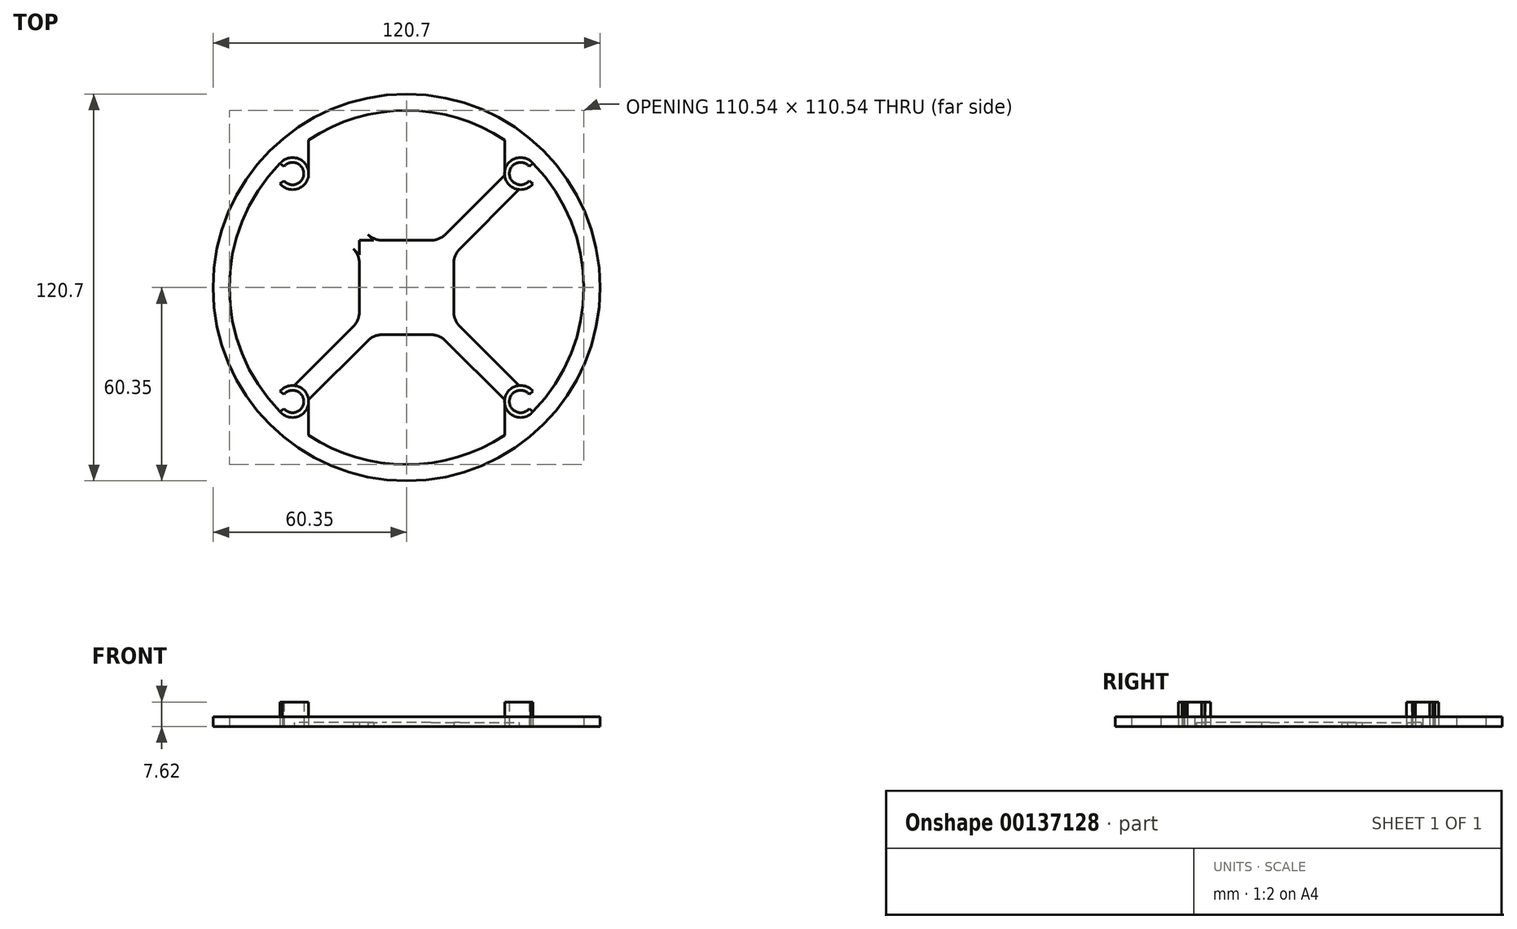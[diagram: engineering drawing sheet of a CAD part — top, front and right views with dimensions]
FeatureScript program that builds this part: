
annotation { "Feature Type Name" : "Feature", "Feature Type Description" : "" }
export const myFeature = defineFeature(function(context is Context, id is Id, definition is map)
    precondition{}
    {
        {
            var Q0;
            Q0=qCreatedBy(makeId("Top.planeOp"),FACE);
            var sketch = newSketch(context, id + "F0", { "sketchPlane" : qUnion([Q0])});
            skLineSegment(sketch, "E0.bottom", {"start": v(35.56, 35.56) * mm, "end": v(-35.56, 35.56) * mm});
            skLineSegment(sketch, "E0.top", {"start": v(35.56, -35.56) * mm, "end": v(-35.56, -35.56) * mm});
            skLineSegment(sketch, "E0.left", {"start": v(35.56, 35.56) * mm, "end": v(35.56, -35.56) * mm});
            skLineSegment(sketch, "E0.right", {"start": v(-35.56, 35.56) * mm, "end": v(-35.56, -35.56) * mm});
            skPoint(sketch, "E0.middle", {"position": v(0, 0) * mm});
            skLineSegment(sketch, "E1", {"start": v(0, 35.56) * mm, "end": v(0, -35.56) * mm, "construction": true});
            skCircle(sketch, "E2", {"center": v(35.56, 35.56) * mm, "radius": 3.5 * mm});
            skCircle(sketch, "E3", {"center": v(35.56, 35.56) * mm, "radius": 5 * mm});
            skLineSegment(sketch, "E4", {"start": v(35.56, 35.56) * mm, "end": v(40.56, 35.56) * mm, "construction": true});
            skLineSegment(sketch, "E5", {"start": v(35.56, 35.56) * mm, "end": v(39.43, 38.74) * mm});
            skLineSegment(sketch, "E6.MirrorCS", {"start": v(35.56, 35.56) * mm, "end": v(39.43, 32.39) * mm});
            skCircle(sketch, "E7.MirrorC", {"center": v(-35.56, 35.56) * mm, "radius": 5 * mm});
            skCircle(sketch, "E8.MirrorC", {"center": v(-35.56, 35.56) * mm, "radius": 3.5 * mm});
            skLineSegment(sketch, "E9.MirrorCS", {"start": v(-35.56, 35.56) * mm, "end": v(-39.43, 32.39) * mm});
            skLineSegment(sketch, "E10.MirrorCS", {"start": v(-35.56, 35.56) * mm, "end": v(-39.43, 38.73) * mm});
            skLineSegment(sketch, "E11.MirrorCS", {"start": v(-35.56, 35.56) * mm, "end": v(-40.56, 35.56) * mm, "construction": true});
            skLineSegment(sketch, "E12.bottom", {"start": v(14.73, 14.73) * mm, "end": v(-14.73, 14.73) * mm});
            skLineSegment(sketch, "E12.top", {"start": v(14.73, -14.73) * mm, "end": v(-14.73, -14.73) * mm});
            skLineSegment(sketch, "E12.left", {"start": v(14.73, 14.73) * mm, "end": v(14.73, -14.73) * mm});
            skLineSegment(sketch, "E12.right", {"start": v(-14.73, 14.73) * mm, "end": v(-14.73, -14.73) * mm});
            skLineSegment(sketch, "E13", {"start": v(-35.56, 0) * mm, "end": v(35.56, 0) * mm, "construction": true});
            skCircle(sketch, "E14.MirrorC", {"center": v(35.56, -35.56) * mm, "radius": 5 * mm});
            skCircle(sketch, "E15.MirrorC", {"center": v(35.56, -35.56) * mm, "radius": 3.5 * mm});
            skLineSegment(sketch, "E16.MirrorCS", {"start": v(35.56, -35.56) * mm, "end": v(39.43, -32.39) * mm});
            skLineSegment(sketch, "E17.MirrorCS", {"start": v(35.56, -35.56) * mm, "end": v(40.56, -35.56) * mm, "construction": true});
            skLineSegment(sketch, "E18.MirrorCS", {"start": v(35.56, -35.56) * mm, "end": v(39.43, -38.74) * mm});
            skCircle(sketch, "E19.MirrorC", {"center": v(-35.56, -35.56) * mm, "radius": 5 * mm});
            skCircle(sketch, "E20.MirrorC", {"center": v(-35.56, -35.56) * mm, "radius": 3.5 * mm});
            skLineSegment(sketch, "E21.MirrorCS", {"start": v(-35.56, -35.56) * mm, "end": v(-39.43, -32.39) * mm});
            skLineSegment(sketch, "E22.MirrorCS", {"start": v(-35.56, -35.56) * mm, "end": v(-40.56, -35.56) * mm, "construction": true});
            skLineSegment(sketch, "E23.MirrorCS", {"start": v(-35.56, -35.56) * mm, "end": v(-39.43, -38.74) * mm});
            skLineSegment(sketch, "E24", {"start": v(0, 0) * mm, "end": v(35.56, 35.56) * mm, "construction": true});
            skLineSegment(sketch, "E25.MirrorCS", {"start": v(0, 0) * mm, "end": v(-35.56, 35.56) * mm, "construction": true});
            skLineSegment(sketch, "E26.MirrorCS", {"start": v(0, 0) * mm, "end": v(35.56, -35.56) * mm, "construction": true});
            skLineSegment(sketch, "E27.MirrorCS", {"start": v(0, 0) * mm, "end": v(-35.56, -35.56) * mm, "construction": true});
            skLineSegment(sketch, "E28", {"start": v(14.73, -10.24) * mm, "end": v(35.07, -30.58) * mm});
            skLineSegment(sketch, "E29.MirrorCS", {"start": v(10.24, -14.73) * mm, "end": v(30.58, -35.07) * mm});
            skLineSegment(sketch, "E30.MirrorCS", {"start": v(10.24, 14.73) * mm, "end": v(30.58, 35.07) * mm});
            skLineSegment(sketch, "E31.MirrorCS", {"start": v(14.73, 10.24) * mm, "end": v(35.07, 30.58) * mm});
            skLineSegment(sketch, "E32.MirrorCS", {"start": v(-10.24, 14.73) * mm, "end": v(-30.58, 35.07) * mm});
            skLineSegment(sketch, "E33.MirrorCS", {"start": v(-14.73, 10.24) * mm, "end": v(-35.07, 30.58) * mm});
            skLineSegment(sketch, "E34.MirrorCS", {"start": v(-14.73, -10.24) * mm, "end": v(-35.07, -30.58) * mm});
            skLineSegment(sketch, "E35.MirrorCS", {"start": v(-10.24, -14.73) * mm, "end": v(-30.58, -35.07) * mm});
            skCircle(sketch, "E36", {"center": v(21.08, 7.61) * mm, "radius": 6.35 * mm});
            skCircle(sketch, "E37.MirrorC", {"center": v(7.61, 21.08) * mm, "radius": 6.35 * mm});
            skCircle(sketch, "E38.MirrorC", {"center": v(21.08, -7.61) * mm, "radius": 6.35 * mm});
            skCircle(sketch, "E39.MirrorC", {"center": v(7.61, -21.08) * mm, "radius": 6.35 * mm});
            skCircle(sketch, "E40.MirrorC", {"center": v(-21.08, 7.61) * mm, "radius": 6.35 * mm});
            skCircle(sketch, "E41.MirrorC", {"center": v(-21.08, -7.61) * mm, "radius": 6.35 * mm});
            skCircle(sketch, "E42.MirrorC", {"center": v(-7.61, -21.08) * mm, "radius": 6.35 * mm});
            skCircle(sketch, "E43.MirrorC", {"center": v(-7.61, 21.08) * mm, "radius": 6.35 * mm});
            skCircle(sketch, "E44", {"center": v(0, 0) * mm, "radius": 55.27 * mm});
            skCircle(sketch, "E45", {"center": v(0, 0) * mm, "radius": 60.35 * mm});
            skLineSegment(sketch, "E46", {"start": v(-30.56, -35.56) * mm, "end": v(-30.56, -46.06) * mm});
            skLineSegment(sketch, "E47", {"start": v(30.56, -35.56) * mm, "end": v(30.56, -46.06) * mm});
            skLineSegment(sketch, "E48.MirrorCS", {"start": v(30.56, 35.56) * mm, "end": v(30.56, 46.06) * mm});
            skLineSegment(sketch, "E49.MirrorCS", {"start": v(-30.56, 35.56) * mm, "end": v(-30.56, 46.06) * mm});
            skSolve(sketch);
        }
        {
            var Q0;
            {var subQ0=sQuery(id+"F0.wireOp",EDGE,"E32.MirrorCS");var subQ9=sQuery(id+"F0.wireOp",EDGE,"E7.MirrorC");var subQ10=makeQuery(id+"F0.imprint","INTERSECT",VERTEX,{"derivedFrom":[subQ9,subQ0]});Q0=makeQuery(id+"F0.imprint","IMPRINT",FACE,{"disambiguationData":[TD([[makeQuery(id+"F0.imprint","IMPRINT",EDGE,{"disambiguationData":[TD([[subQ10,-1.0]])],"derivedFrom":subQ9}),1.0]])]});}
            var Q1;
            {var subQ4=sQuery(id+"F0.wireOp",EDGE,"E12.bottom");var subQ7=sQuery(id+"F0.wireOp",EDGE,"E12.left");var subQ14=makeQuery(id+"F0.imprint","INTERSECT",VERTEX,{"derivedFrom":[subQ4,subQ7]});Q1=makeQuery(id+"F0.imprint","IMPRINT",FACE,{"disambiguationData":[TD([[makeQuery(id+"F0.imprint","IMPRINT",EDGE,{"disambiguationData":[TD([[subQ14,-1.0]])],"derivedFrom":subQ4}),1.0]])]});}
            var Q2;
            {var subQ3=sQuery(id+"F0.wireOp",EDGE,"E30.MirrorCS");var subQ9=sQuery(id+"F0.wireOp",EDGE,"E3");var subQ10=makeQuery(id+"F0.imprint","INTERSECT",VERTEX,{"derivedFrom":[subQ9,subQ3]});Q2=makeQuery(id+"F0.imprint","IMPRINT",FACE,{"disambiguationData":[TD([[makeQuery(id+"F0.imprint","IMPRINT",EDGE,{"disambiguationData":[TD([[subQ10,-1.0]])],"derivedFrom":subQ9}),-1.0]])]});}
            var Q3;
            {var subQ5=sQuery(id+"F0.wireOp",EDGE,"E12.left");var subQ6=sQuery(id+"F0.wireOp",EDGE,"E12.top");var subQ7=makeQuery(id+"F0.imprint","INTERSECT",VERTEX,{"derivedFrom":[subQ6,subQ5]});Q3=makeQuery(id+"F0.imprint","IMPRINT",FACE,{"disambiguationData":[TD([[makeQuery(id+"F0.imprint","IMPRINT",EDGE,{"disambiguationData":[TD([[subQ7,-1.0]])],"derivedFrom":subQ6}),1.0]])]});}
            var Q4;
            {var subQ1=sQuery(id+"F0.wireOp",EDGE,"E12.right");var subQ8=sQuery(id+"F0.wireOp",EDGE,"E12.top");var subQ9=makeQuery(id+"F0.imprint","INTERSECT",VERTEX,{"derivedFrom":[subQ8,subQ1]});Q4=makeQuery(id+"F0.imprint","IMPRINT",FACE,{"disambiguationData":[TD([[makeQuery(id+"F0.imprint","IMPRINT",EDGE,{"disambiguationData":[TD([[subQ9,1.0]])],"derivedFrom":subQ8}),1.0]])]});}
            var Q5;
            {var subQ0=sQuery(id+"F0.wireOp",EDGE,"E35.MirrorCS");var subQ1=sQuery(id+"F0.wireOp",EDGE,"E12.top");var subQ2=makeQuery(id+"F0.imprint","INTERSECT",VERTEX,{"derivedFrom":[subQ1,subQ0]});Q5=makeQuery(id+"F0.imprint","IMPRINT",FACE,{"disambiguationData":[TD([[makeQuery(id+"F0.imprint","IMPRINT",EDGE,{"disambiguationData":[TD([[subQ2,1.0]])],"derivedFrom":subQ1}),1.0]])]});}
            var Q6;
            {var subQ0=sQuery(id+"F0.wireOp",EDGE,"E34.MirrorCS");var subQ1=sQuery(id+"F0.wireOp",EDGE,"E12.right");var subQ2=makeQuery(id+"F0.imprint","INTERSECT",VERTEX,{"derivedFrom":[subQ1,subQ0]});Q6=makeQuery(id+"F0.imprint","IMPRINT",FACE,{"disambiguationData":[TD([[makeQuery(id+"F0.imprint","IMPRINT",EDGE,{"disambiguationData":[TD([[subQ2,1.0]])],"derivedFrom":subQ1}),-1.0]])]});}
            var Q7;
            {var subQ0=sQuery(id+"F0.wireOp",EDGE,"E29.MirrorCS");var subQ1=sQuery(id+"F0.wireOp",EDGE,"E12.top");var subQ2=makeQuery(id+"F0.imprint","INTERSECT",VERTEX,{"derivedFrom":[subQ1,subQ0]});Q7=makeQuery(id+"F0.imprint","IMPRINT",FACE,{"disambiguationData":[TD([[makeQuery(id+"F0.imprint","IMPRINT",EDGE,{"disambiguationData":[TD([[subQ2,-1.0]])],"derivedFrom":subQ1}),1.0]])]});}
            var Q8;
            {var subQ0=sQuery(id+"F0.wireOp",EDGE,"E28");var subQ1=sQuery(id+"F0.wireOp",EDGE,"E12.left");var subQ2=makeQuery(id+"F0.imprint","INTERSECT",VERTEX,{"derivedFrom":[subQ1,subQ0]});Q8=makeQuery(id+"F0.imprint","IMPRINT",FACE,{"disambiguationData":[TD([[makeQuery(id+"F0.imprint","IMPRINT",EDGE,{"disambiguationData":[TD([[subQ2,1.0]])],"derivedFrom":subQ1}),1.0]])]});}
            var Q9;
            {var subQ0=sQuery(id+"F0.wireOp",EDGE,"E31.MirrorCS");var subQ1=sQuery(id+"F0.wireOp",EDGE,"E12.left");var subQ2=makeQuery(id+"F0.imprint","INTERSECT",VERTEX,{"derivedFrom":[subQ1,subQ0]});Q9=makeQuery(id+"F0.imprint","IMPRINT",FACE,{"disambiguationData":[TD([[makeQuery(id+"F0.imprint","IMPRINT",EDGE,{"disambiguationData":[TD([[subQ2,-1.0]])],"derivedFrom":subQ1}),1.0]])]});}
            var Q10;
            {var subQ0=sQuery(id+"F0.wireOp",EDGE,"E30.MirrorCS");var subQ1=sQuery(id+"F0.wireOp",EDGE,"E12.bottom");var subQ2=makeQuery(id+"F0.imprint","INTERSECT",VERTEX,{"derivedFrom":[subQ1,subQ0]});Q10=makeQuery(id+"F0.imprint","IMPRINT",FACE,{"disambiguationData":[TD([[makeQuery(id+"F0.imprint","IMPRINT",EDGE,{"disambiguationData":[TD([[subQ2,-1.0]])],"derivedFrom":subQ1}),-1.0]])]});}
            var Q11;
            {var subQ0=sQuery(id+"F0.wireOp",EDGE,"E32.MirrorCS");var subQ1=sQuery(id+"F0.wireOp",EDGE,"E12.bottom");var subQ2=makeQuery(id+"F0.imprint","INTERSECT",VERTEX,{"derivedFrom":[subQ1,subQ0]});Q11=makeQuery(id+"F0.imprint","IMPRINT",FACE,{"disambiguationData":[TD([[makeQuery(id+"F0.imprint","IMPRINT",EDGE,{"disambiguationData":[TD([[subQ2,1.0]])],"derivedFrom":subQ1}),-1.0]])]});}
            var Q12;
            {var subQ0=sQuery(id+"F0.wireOp",EDGE,"E33.MirrorCS");var subQ1=sQuery(id+"F0.wireOp",EDGE,"E12.right");var subQ2=makeQuery(id+"F0.imprint","INTERSECT",VERTEX,{"derivedFrom":[subQ1,subQ0]});Q12=makeQuery(id+"F0.imprint","IMPRINT",FACE,{"disambiguationData":[TD([[makeQuery(id+"F0.imprint","IMPRINT",EDGE,{"disambiguationData":[TD([[subQ2,-1.0]])],"derivedFrom":subQ1}),-1.0]])]});}
            extrude(context, id + "F1", {"entities" : qUnion([Q0, Q1, Q2, Q3, Q4, Q5, Q6, Q7, Q8, Q9, Q10, Q11, Q12]), "depth" : 1.27 * mm});
        }
        {
            var Q0;
            {var subQ1=sQuery(id+"F0.wireOp",EDGE,"E0.bottom");var subQ6=sQuery(id+"F0.wireOp",EDGE,"E7.MirrorC");var subQ8=makeQuery(id+"F0.imprint","INTERSECT",VERTEX,{"derivedFrom":[subQ1,subQ6]});Q0=makeQuery(id+"F0.imprint","IMPRINT",FACE,{"disambiguationData":[TD([[makeQuery(id+"F0.imprint","IMPRINT",EDGE,{"disambiguationData":[TD([[subQ8,-1.0]])],"derivedFrom":subQ1}),-1.0]])]});}
            var Q1;
            {var subQ0=sQuery(id+"F0.wireOp",EDGE,"E7.MirrorC");var subQ2=sQuery(id+"F0.wireOp",EDGE,"E0.bottom");var subQ3=makeQuery(id+"F0.imprint","INTERSECT",VERTEX,{"derivedFrom":[subQ2,subQ0]});Q1=makeQuery(id+"F0.imprint","IMPRINT",FACE,{"disambiguationData":[TD([[makeQuery(id+"F0.imprint","IMPRINT",EDGE,{"disambiguationData":[TD([[subQ3,-1.0]])],"derivedFrom":subQ2}),1.0]])]});}
            var Q2;
            {var subQ0=sQuery(id+"F0.wireOp",EDGE,"E8.MirrorC");var subQ1=sQuery(id+"F0.wireOp",EDGE,"E0.right");var subQ2=makeQuery(id+"F0.imprint","INTERSECT",VERTEX,{"derivedFrom":[subQ1,subQ0]});Q2=makeQuery(id+"F0.imprint","IMPRINT",FACE,{"disambiguationData":[TD([[makeQuery(id+"F0.imprint","IMPRINT",EDGE,{"disambiguationData":[TD([[subQ2,-1.0]])],"derivedFrom":subQ1}),-1.0]])]});}
            var Q3;
            {var subQ1=sQuery(id+"F0.wireOp",EDGE,"E0.bottom");var subQ5=sQuery(id+"F0.wireOp",EDGE,"E2");var subQ6=makeQuery(id+"F0.imprint","INTERSECT",VERTEX,{"derivedFrom":[subQ1,subQ5]});Q3=makeQuery(id+"F0.imprint","IMPRINT",FACE,{"disambiguationData":[TD([[makeQuery(id+"F0.imprint","IMPRINT",EDGE,{"disambiguationData":[TD([[subQ6,-1.0]])],"derivedFrom":subQ1}),-1.0]])]});}
            var Q4;
            {var subQ0=sQuery(id+"F0.wireOp",EDGE,"E2");var subQ1=sQuery(id+"F0.wireOp",EDGE,"E0.bottom");var subQ2=makeQuery(id+"F0.imprint","INTERSECT",VERTEX,{"derivedFrom":[subQ1,subQ0]});Q4=makeQuery(id+"F0.imprint","IMPRINT",FACE,{"disambiguationData":[TD([[makeQuery(id+"F0.imprint","IMPRINT",EDGE,{"disambiguationData":[TD([[subQ2,-1.0]])],"derivedFrom":subQ1}),1.0]])]});}
            var Q5;
            {var subQ0=sQuery(id+"F0.wireOp",EDGE,"E2");var subQ1=sQuery(id+"F0.wireOp",EDGE,"E0.left");var subQ2=makeQuery(id+"F0.imprint","INTERSECT",VERTEX,{"derivedFrom":[subQ1,subQ0]});Q5=makeQuery(id+"F0.imprint","IMPRINT",FACE,{"disambiguationData":[TD([[makeQuery(id+"F0.imprint","IMPRINT",EDGE,{"disambiguationData":[TD([[subQ2,-1.0]])],"derivedFrom":subQ1}),1.0]])]});}
            var Q6;
            {var subQ0=sQuery(id+"F0.wireOp",EDGE,"E14.MirrorC");var subQ1=sQuery(id+"F0.wireOp",EDGE,"E0.left");var subQ2=makeQuery(id+"F0.imprint","INTERSECT",VERTEX,{"derivedFrom":[subQ1,subQ0]});Q6=makeQuery(id+"F0.imprint","IMPRINT",FACE,{"disambiguationData":[TD([[makeQuery(id+"F0.imprint","IMPRINT",EDGE,{"disambiguationData":[TD([[subQ2,-1.0]])],"derivedFrom":subQ1}),1.0]])]});}
            var Q7;
            {var subQ3=sQuery(id+"F0.wireOp",EDGE,"E0.top");var subQ7=sQuery(id+"F0.wireOp",EDGE,"E15.MirrorC");var subQ9=makeQuery(id+"F0.imprint","INTERSECT",VERTEX,{"derivedFrom":[subQ3,subQ7]});Q7=makeQuery(id+"F0.imprint","IMPRINT",FACE,{"disambiguationData":[TD([[makeQuery(id+"F0.imprint","IMPRINT",EDGE,{"disambiguationData":[TD([[subQ9,-1.0]])],"derivedFrom":subQ3}),-1.0]])]});}
            var Q8;
            {var subQ0=sQuery(id+"F0.wireOp",EDGE,"E15.MirrorC");var subQ1=sQuery(id+"F0.wireOp",EDGE,"E0.top");var subQ2=makeQuery(id+"F0.imprint","INTERSECT",VERTEX,{"derivedFrom":[subQ1,subQ0]});Q8=makeQuery(id+"F0.imprint","IMPRINT",FACE,{"disambiguationData":[TD([[makeQuery(id+"F0.imprint","IMPRINT",EDGE,{"disambiguationData":[TD([[subQ2,-1.0]])],"derivedFrom":subQ1}),1.0]])]});}
            var Q9;
            {var subQ1=sQuery(id+"F0.wireOp",EDGE,"E0.top");var subQ6=sQuery(id+"F0.wireOp",EDGE,"E19.MirrorC");var subQ8=makeQuery(id+"F0.imprint","INTERSECT",VERTEX,{"derivedFrom":[subQ1,subQ6]});Q9=makeQuery(id+"F0.imprint","IMPRINT",FACE,{"disambiguationData":[TD([[makeQuery(id+"F0.imprint","IMPRINT",EDGE,{"disambiguationData":[TD([[subQ8,-1.0]])],"derivedFrom":subQ1}),1.0]])]});}
            var Q10;
            {var subQ0=sQuery(id+"F0.wireOp",EDGE,"E19.MirrorC");var subQ3=sQuery(id+"F0.wireOp",EDGE,"E0.top");var subQ4=makeQuery(id+"F0.imprint","INTERSECT",VERTEX,{"derivedFrom":[subQ3,subQ0]});Q10=makeQuery(id+"F0.imprint","IMPRINT",FACE,{"disambiguationData":[TD([[makeQuery(id+"F0.imprint","IMPRINT",EDGE,{"disambiguationData":[TD([[subQ4,-1.0]])],"derivedFrom":subQ3}),-1.0]])]});}
            var Q11;
            {var subQ0=sQuery(id+"F0.wireOp",EDGE,"E19.MirrorC");var subQ1=sQuery(id+"F0.wireOp",EDGE,"E0.right");var subQ2=makeQuery(id+"F0.imprint","INTERSECT",VERTEX,{"derivedFrom":[subQ1,subQ0]});Q11=makeQuery(id+"F0.imprint","IMPRINT",FACE,{"disambiguationData":[TD([[makeQuery(id+"F0.imprint","IMPRINT",EDGE,{"disambiguationData":[TD([[subQ2,-1.0]])],"derivedFrom":subQ1}),-1.0]])]});}
            extrude(context, id + "F2", {"entities" : qUnion([Q0, Q1, Q2, Q3, Q4, Q5, Q6, Q7, Q8, Q9, Q10, Q11]), "operationType" : NewBodyOperationType.ADD, "depth" : 7.62 * mm});
        }
        {
            var Q0;
            Q0=makeQuery(id+"F0.imprint","IMPRINT",FACE,{"disambiguationData":[TD([[makeQuery(id+"F0.imprint","IMPRINT",EDGE,{"derivedFrom":sQuery(id+"F0.wireOp",EDGE,"E45")}),1.0]])]});
            var Q1;
            {var subQ0=sQuery(id+"F0.wireOp",EDGE,"E46");Q1=makeQuery(id+"F0.imprint","IMPRINT",FACE,{"disambiguationData":[TD([[makeQuery(id+"F0.imprint","IMPRINT",EDGE,{"derivedFrom":subQ0}),-1.0]])]});}
            var Q2;
            {var subQ0=sQuery(id+"F0.wireOp",EDGE,"E49.MirrorCS");Q2=makeQuery(id+"F0.imprint","IMPRINT",FACE,{"disambiguationData":[TD([[makeQuery(id+"F0.imprint","IMPRINT",EDGE,{"derivedFrom":subQ0}),1.0]])]});}
            var Q3;
            {var subQ0=sQuery(id+"F0.wireOp",EDGE,"E48.MirrorCS");Q3=makeQuery(id+"F0.imprint","IMPRINT",FACE,{"disambiguationData":[TD([[makeQuery(id+"F0.imprint","IMPRINT",EDGE,{"derivedFrom":subQ0}),-1.0]])]});}
            var Q4;
            {var subQ0=sQuery(id+"F0.wireOp",EDGE,"E47");Q4=makeQuery(id+"F0.imprint","IMPRINT",FACE,{"disambiguationData":[TD([[makeQuery(id+"F0.imprint","IMPRINT",EDGE,{"derivedFrom":subQ0}),1.0]])]});}
            extrude(context, id + "F3", {"entities" : qUnion([Q0, Q1, Q2, Q3, Q4]), "depth" : 3 * mm});
        }
    });
